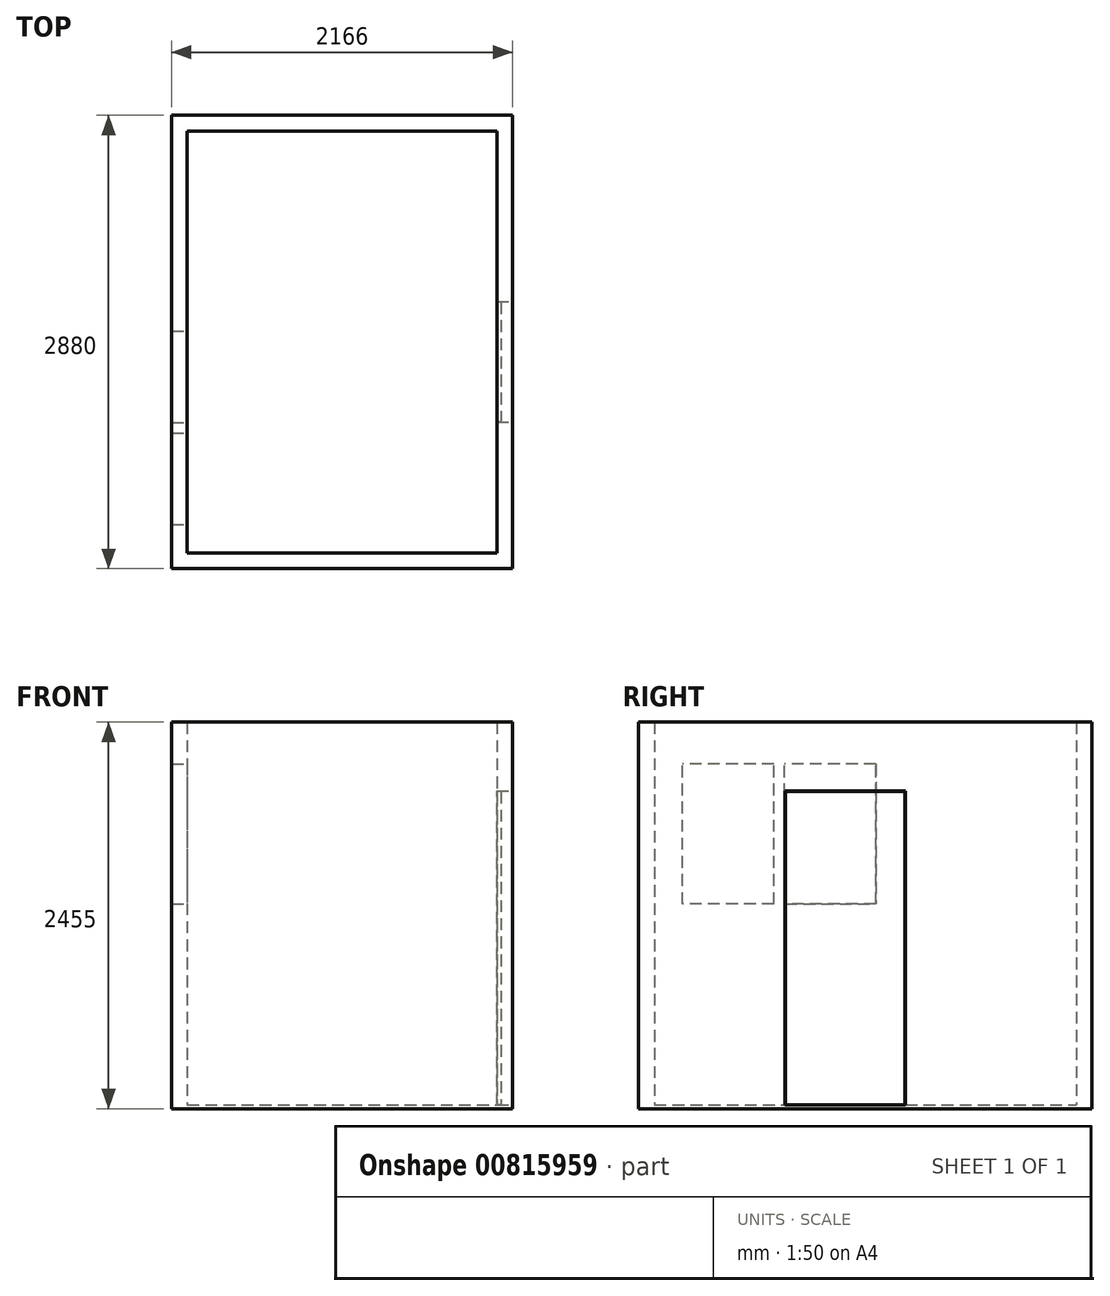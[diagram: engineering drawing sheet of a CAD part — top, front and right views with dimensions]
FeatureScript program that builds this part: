
annotation { "Feature Type Name" : "Feature", "Feature Type Description" : "" }
export const myFeature = defineFeature(function(context is Context, id is Id, definition is map)
    precondition{}
    {
        {
            var Q0;
            Q0=qCreatedBy(makeId("Top.planeOp"),FACE);
            var sketch = newSketch(context, id + "F0", { "sketchPlane" : qUnion([Q0])});
            skLineSegment(sketch, "E0.bottom", {"start": v(-1966, -2680) * mm, "end": v(0, -2680) * mm});
            skLineSegment(sketch, "E0.top", {"start": v(-1966, 0) * mm, "end": v(0, 0) * mm});
            skLineSegment(sketch, "E0.left", {"start": v(-1966, -2680) * mm, "end": v(-1966, 0) * mm});
            skLineSegment(sketch, "E0.right", {"start": v(0, -2680) * mm, "end": v(0, 0) * mm});
            skLineSegment(sketch, "E1.bottom", {"start": v(-2066, -2780) * mm, "end": v(100, -2780) * mm});
            skLineSegment(sketch, "E1.top", {"start": v(-2066, 100) * mm, "end": v(100, 100) * mm});
            skLineSegment(sketch, "E1.left", {"start": v(-2066, -2780) * mm, "end": v(-2066, 100) * mm});
            skLineSegment(sketch, "E1.right", {"start": v(100, -2780) * mm, "end": v(100, 100) * mm});
            skLineSegment(sketch, "E2", {"start": v(0, -1850) * mm, "end": v(100, -1850) * mm});
            skLineSegment(sketch, "E3", {"start": v(0, -1085) * mm, "end": v(100, -1085) * mm});
            skLineSegment(sketch, "E4", {"start": v(-1966, -1272) * mm, "end": v(-2066, -1272) * mm});
            skLineSegment(sketch, "E5", {"start": v(-1966, -1852) * mm, "end": v(-2066, -1852) * mm});
            skLineSegment(sketch, "E6", {"start": v(-1966, -1920) * mm, "end": v(-2066, -1920) * mm});
            skLineSegment(sketch, "E7", {"start": v(-1966, -2500) * mm, "end": v(-2066, -2500) * mm});
            skSolve(sketch);
        }
        {
            var Q0;
            {var subQ1=sQuery(id+"F0.wireOp",EDGE,"E0.bottom");Q0=makeQuery(id+"F0.imprint","IMPRINT",FACE,{"disambiguationData":[TD([[makeQuery(id+"F0.imprint","IMPRINT",EDGE,{"derivedFrom":subQ1}),-1.0]])]});}
            var Q1;
            {var subQ0=sQuery(id+"F0.wireOp",EDGE,"E6");Q1=makeQuery(id+"F0.imprint","IMPRINT",FACE,{"disambiguationData":[TD([[makeQuery(id+"F0.imprint","IMPRINT",EDGE,{"derivedFrom":subQ0}),1.0]])]});}
            var Q2;
            {var subQ0=sQuery(id+"F0.wireOp",EDGE,"E5");Q2=makeQuery(id+"F0.imprint","IMPRINT",FACE,{"disambiguationData":[TD([[makeQuery(id+"F0.imprint","IMPRINT",EDGE,{"derivedFrom":subQ0}),1.0]])]});}
            var Q3;
            {var subQ0=sQuery(id+"F0.wireOp",EDGE,"E4");Q3=makeQuery(id+"F0.imprint","IMPRINT",FACE,{"disambiguationData":[TD([[makeQuery(id+"F0.imprint","IMPRINT",EDGE,{"derivedFrom":subQ0}),1.0]])]});}
            var Q4;
            {var subQ0=sQuery(id+"F0.wireOp",EDGE,"E2");Q4=makeQuery(id+"F0.imprint","IMPRINT",FACE,{"disambiguationData":[TD([[makeQuery(id+"F0.imprint","IMPRINT",EDGE,{"derivedFrom":subQ0}),1.0]])]});}
            var Q5;
            {var subQ1=sQuery(id+"F0.wireOp",EDGE,"E0.top");Q5=makeQuery(id+"F0.imprint","IMPRINT",FACE,{"disambiguationData":[TD([[makeQuery(id+"F0.imprint","IMPRINT",EDGE,{"derivedFrom":subQ1}),1.0]])]});}
            extrude(context, id + "F1", {"entities" : qUnion([Q0, Q1, Q2, Q3, Q4, Q5]), "depth" : 2430 * mm, "offsetDistance" : 25 * mm});
        }
        {
            var Q0;
            Q0=makeQuery(id+"F1.opExtrude","SWEPT_FACE",FACE,{"disambiguationData":[OSD([sQuery(id+"F0.wireOp",EDGE,"E0.left")])]});
            var sketch = newSketch(context, id + "F2", { "sketchPlane" : qUnion([Q0])});
            skLineSegment(sketch, "E8.bottom", {"start": v(-2500, 2165) * mm, "end": v(-1920, 2165) * mm});
            skLineSegment(sketch, "E8.top", {"start": v(-2500, 1275) * mm, "end": v(-1920, 1275) * mm});
            skLineSegment(sketch, "E8.left", {"start": v(-2500, 2165) * mm, "end": v(-2500, 1275) * mm});
            skLineSegment(sketch, "E8.right", {"start": v(-1920, 2165) * mm, "end": v(-1920, 1275) * mm});
            skLineSegment(sketch, "E9.bottom", {"start": v(-1852, 2165) * mm, "end": v(-1272, 2165) * mm});
            skLineSegment(sketch, "E9.top", {"start": v(-1852, 1275) * mm, "end": v(-1272, 1275) * mm});
            skLineSegment(sketch, "E9.left", {"start": v(-1852, 2165) * mm, "end": v(-1852, 1275) * mm});
            skLineSegment(sketch, "E9.right", {"start": v(-1272, 2165) * mm, "end": v(-1272, 1275) * mm});
            skSolve(sketch);
        }
        {
            var Q0;
            Q0=makeQuery(id+"F2.imprint","IMPRINT",FACE,{"disambiguationData":[TD([[makeQuery(id+"F2.imprint","IMPRINT",EDGE,{"derivedFrom":sQuery(id+"F2.wireOp",EDGE,"E9.bottom")}),-1.0]])]});
            var Q1;
            Q1=makeQuery(id+"F2.imprint","IMPRINT",FACE,{"disambiguationData":[TD([[makeQuery(id+"F2.imprint","IMPRINT",EDGE,{"derivedFrom":sQuery(id+"F2.wireOp",EDGE,"E8.bottom")}),-1.0]])]});
            extrude(context, id + "F3", {"entities" : qUnion([Q0, Q1]), "operationType" : NewBodyOperationType.REMOVE, "endBound" : BoundingType.THROUGH_ALL, "oppositeDirection" : true, "depth" : 25 * mm, "offsetDistance" : 25 * mm});
        }
        {
            var Q0;
            Q0=makeQuery(id+"F1.opExtrude","SWEPT_FACE",FACE,{"disambiguationData":[OSD([sQuery(id+"F0.wireOp",EDGE,"E1.right")])]});
            var sketch = newSketch(context, id + "F4", { "sketchPlane" : qUnion([Q0])});
            skLineSegment(sketch, "E10.bottom", {"start": v(-1850, 0) * mm, "end": v(-1085, 0) * mm});
            skLineSegment(sketch, "E10.top", {"start": v(-1850, 1994) * mm, "end": v(-1085, 1994) * mm});
            skLineSegment(sketch, "E10.left", {"start": v(-1850, 0) * mm, "end": v(-1850, 1994) * mm});
            skLineSegment(sketch, "E10.right", {"start": v(-1085, 0) * mm, "end": v(-1085, 1994) * mm});
            skSolve(sketch);
        }
        {
            var Q0;
            Q0=makeQuery(id+"F4.imprint","IMPRINT",FACE,{"disambiguationData":[TD([[makeQuery(id+"F4.imprint","IMPRINT",EDGE,{"derivedFrom":sQuery(id+"F4.wireOp",EDGE,"E10.bottom")}),1.0]])]});
            extrude(context, id + "F5", {"entities" : qUnion([Q0]), "operationType" : NewBodyOperationType.REMOVE, "endBound" : BoundingType.UP_TO_NEXT, "oppositeDirection" : true, "depth" : 25 * mm, "offsetDistance" : 25 * mm});
        }
        {
            var Q0;
            Q0=makeQuery(id+"F1.opExtrude","SWEPT_FACE",FACE,{"disambiguationData":[OSD([sQuery(id+"F0.wireOp",EDGE,"E0.right")])]});
            var sketch = newSketch(context, id + "F6", { "sketchPlane" : qUnion([Q0])});
            skPoint(sketch, "E11.0", {"position": v(1085, 0) * mm});
            skPoint(sketch, "E12.0", {"position": v(1850, 0) * mm});
            skLineSegment(sketch, "E13.0", {"start": v(1850, 1994) * mm, "end": v(1085, 1994) * mm, "construction": true});
            skLineSegment(sketch, "E14.bottom", {"start": v(1087.5, 1989) * mm, "end": v(1847.5, 1989) * mm});
            skLineSegment(sketch, "E14.top", {"start": v(1087.5, 0) * mm, "end": v(1847.5, 0) * mm});
            skLineSegment(sketch, "E14.left", {"start": v(1087.5, 1989) * mm, "end": v(1087.5, 0) * mm});
            skLineSegment(sketch, "E14.right", {"start": v(1847.5, 1989) * mm, "end": v(1847.5, 0) * mm});
            skSolve(sketch);
        }
        {
            var Q0;
            Q0=makeQuery(id+"F6.imprint","IMPRINT",FACE,{"disambiguationData":[TD([[makeQuery(id+"F6.imprint","IMPRINT",EDGE,{"derivedFrom":sQuery(id+"F6.wireOp",EDGE,"E14.bottom")}),-1.0]])]});
            extrude(context, id + "F7", {"entities" : qUnion([Q0]), "oppositeDirection" : true, "depth" : 25 * mm, "offsetDistance" : 25 * mm});
        }
        {
            var Q0;
            Q0=qSketchRegion(id+"F0",true);
            var Q1;
            {var subQ3=sQuery(id+"F0.wireOp",EDGE,"E0.bottom");Q1=makeQuery(id+"F0.imprint","IMPRINT",FACE,{"disambiguationData":[TD([[makeQuery(id+"F0.imprint","IMPRINT",EDGE,{"derivedFrom":subQ3}),1.0]])]});}
            extrude(context, id + "F8", {"entities" : qUnion([Q0, Q1]), "operationType" : NewBodyOperationType.ADD, "oppositeDirection" : true, "depth" : 25 * mm, "offsetDistance" : 25 * mm});
        }
    });
